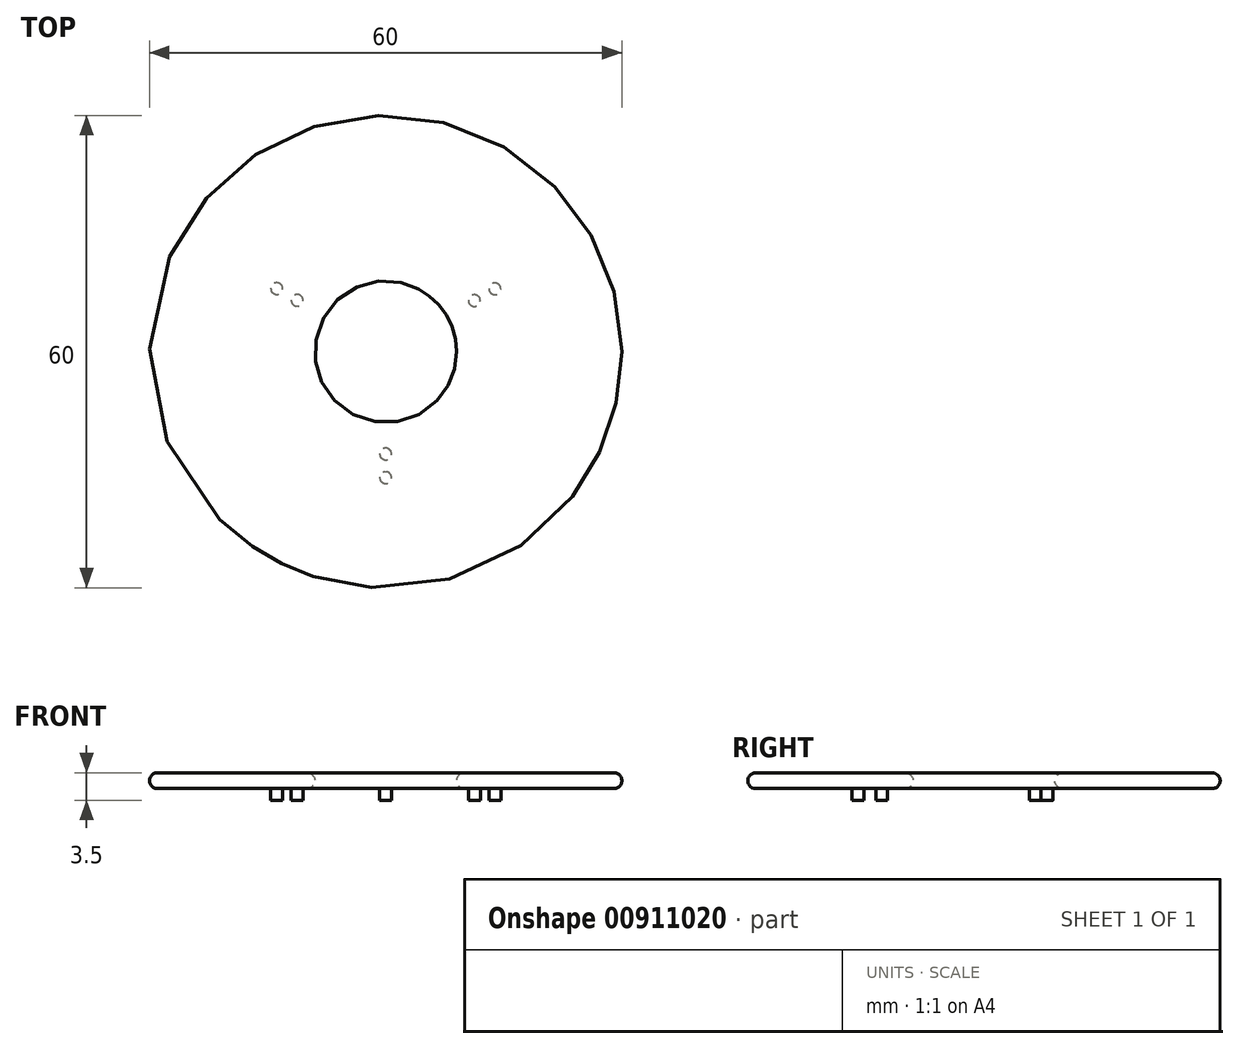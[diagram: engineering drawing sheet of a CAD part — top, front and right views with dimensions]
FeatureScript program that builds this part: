
annotation { "Feature Type Name" : "Feature", "Feature Type Description" : "" }
export const myFeature = defineFeature(function(context is Context, id is Id, definition is map)
    precondition{}
    {
        {
            var Q0;
            Q0=qCreatedBy(makeId("Top.planeOp"),FACE);
            var sketch = newSketch(context, id + "F0", { "sketchPlane" : qUnion([Q0])});
            skCircle(sketch, "E0", {"center": v(0, 0) * mm, "radius": 30 * mm});
            skCircle(sketch, "E1", {"center": v(0, 0) * mm, "radius": 9 * mm});
            skSolve(sketch);
        }
        {
            var Q0;
            Q0=makeQuery(id+"F0.imprint","IMPRINT",FACE,{"disambiguationData":[TD([[makeQuery(id+"F0.imprint","IMPRINT",EDGE,{"derivedFrom":sQuery(id+"F0.wireOp",EDGE,"E0")}),1.0]])]});
            extrude(context, id + "F1", {"entities" : qUnion([Q0]), "depth" : 2 * mm, "offsetDistance" : 25 * mm});
        }
        {
            var Q0;
            Q0=makeQuery(id+"F1.opExtrude","CAP_EDGE",EDGE,{"disambiguationData":[OSD([sQuery(id+"F0.wireOp",EDGE,"E1")])],"isStart":false});
            var Q1;
            Q1=makeQuery(id+"F1.opExtrude","CAP_EDGE",EDGE,{"disambiguationData":[OSD([sQuery(id+"F0.wireOp",EDGE,"E1")])],"isStart":true});
            var Q2;
            Q2=makeQuery(id+"F1.opExtrude","CAP_EDGE",EDGE,{"disambiguationData":[OSD([sQuery(id+"F0.wireOp",EDGE,"E0")])],"isStart":true});
            var Q3;
            Q3=makeQuery(id+"F1.opExtrude","CAP_EDGE",EDGE,{"disambiguationData":[OSD([sQuery(id+"F0.wireOp",EDGE,"E0")])],"isStart":false});
            fillet(context, id + "F2", {"entities" : qUnion([Q0, Q1, Q2, Q3]), "tangentPropagation" : true, "radius" : 1 * mm, "defaultsChanged" : false, "vertexSettings" : [], "allowEdgeOverflow" : false});
        }
        {
            var Q0;
            Q0=qCreatedBy(makeId("Top.planeOp"),FACE);
            var sketch = newSketch(context, id + "F3", { "sketchPlane" : qUnion([Q0])});
            skCircle(sketch, "E2.cCircle", {"center": v(0, 0) * mm, "radius": 13 * mm, "construction": true});
            skLineSegment(sketch, "E2.0", {"start": v(11.26, 6.49) * mm, "end": v(-0.01, -13) * mm});
            skLineSegment(sketch, "E2.1", {"start": v(-0.01, -13) * mm, "end": v(-11.25, 6.51) * mm});
            skLineSegment(sketch, "E2.2", {"start": v(-11.25, 6.51) * mm, "end": v(11.26, 6.49) * mm});
            skCircle(sketch, "E3", {"center": v(-11.25, 6.51) * mm, "radius": 0.75 * mm});
            skCircle(sketch, "E4", {"center": v(11.26, 6.49) * mm, "radius": 0.75 * mm});
            skCircle(sketch, "E5", {"center": v(-0.01, -13) * mm, "radius": 0.75 * mm});
            skCircle(sketch, "E6.cCircle", {"center": v(0, 0) * mm, "radius": 16 * mm, "construction": true});
            skLineSegment(sketch, "E6.0", {"start": v(13.86, 7.99) * mm, "end": v(-0.01, -16) * mm});
            skLineSegment(sketch, "E6.1", {"start": v(-0.01, -16) * mm, "end": v(-13.85, 8.01) * mm});
            skLineSegment(sketch, "E6.2", {"start": v(-13.85, 8.01) * mm, "end": v(13.86, 7.99) * mm});
            skCircle(sketch, "E7", {"center": v(-13.85, 8.01) * mm, "radius": 0.75 * mm});
            skCircle(sketch, "E8", {"center": v(13.86, 7.99) * mm, "radius": 0.75 * mm});
            skCircle(sketch, "E9", {"center": v(-0.01, -16) * mm, "radius": 0.75 * mm});
            skSolve(sketch);
        }
        {
            var Q0;
            {var subQ0=sQuery(id+"F3.wireOp",EDGE,"E6.2");var subQ1=sQuery(id+"F3.wireOp",EDGE,"E6.0");var subQ2=makeQuery(id+"F3.imprint","INTERSECT",VERTEX,{"derivedFrom":[subQ1,subQ0]});Q0=makeQuery(id+"F3.imprint","IMPRINT",FACE,{"disambiguationData":[TD([[makeQuery(id+"F3.imprint","IMPRINT",EDGE,{"disambiguationData":[TD([[subQ2,-1.0]])],"derivedFrom":subQ1}),1.0]])]});}
            var Q1;
            {var subQ0=sQuery(id+"F3.wireOp",EDGE,"E2.2");var subQ1=sQuery(id+"F3.wireOp",EDGE,"E2.0");var subQ2=makeQuery(id+"F3.imprint","INTERSECT",VERTEX,{"derivedFrom":[subQ1,subQ0]});Q1=makeQuery(id+"F3.imprint","IMPRINT",FACE,{"disambiguationData":[TD([[makeQuery(id+"F3.imprint","IMPRINT",EDGE,{"disambiguationData":[TD([[subQ2,-1.0]])],"derivedFrom":subQ1}),1.0]])]});}
            var Q2;
            {var subQ0=sQuery(id+"F3.wireOp",EDGE,"E6.2");var subQ1=sQuery(id+"F3.wireOp",EDGE,"E6.1");var subQ2=makeQuery(id+"F3.imprint","INTERSECT",VERTEX,{"derivedFrom":[subQ1,subQ0]});Q2=makeQuery(id+"F3.imprint","IMPRINT",FACE,{"disambiguationData":[TD([[makeQuery(id+"F3.imprint","IMPRINT",EDGE,{"disambiguationData":[TD([[subQ2,1.0]])],"derivedFrom":subQ1}),-1.0]])]});}
            var Q3;
            {var subQ0=sQuery(id+"F3.wireOp",EDGE,"E6.2");var subQ1=sQuery(id+"F3.wireOp",EDGE,"E6.1");var subQ2=makeQuery(id+"F3.imprint","INTERSECT",VERTEX,{"derivedFrom":[subQ1,subQ0]});Q3=makeQuery(id+"F3.imprint","IMPRINT",FACE,{"disambiguationData":[TD([[makeQuery(id+"F3.imprint","IMPRINT",EDGE,{"disambiguationData":[TD([[subQ2,1.0]])],"derivedFrom":subQ1}),1.0]])]});}
            var Q4;
            {var subQ0=sQuery(id+"F3.wireOp",EDGE,"E2.2");var subQ1=sQuery(id+"F3.wireOp",EDGE,"E2.1");var subQ2=makeQuery(id+"F3.imprint","INTERSECT",VERTEX,{"derivedFrom":[subQ1,subQ0]});Q4=makeQuery(id+"F3.imprint","IMPRINT",FACE,{"disambiguationData":[TD([[makeQuery(id+"F3.imprint","IMPRINT",EDGE,{"disambiguationData":[TD([[subQ2,1.0]])],"derivedFrom":subQ1}),1.0]])]});}
            var Q5;
            {var subQ0=sQuery(id+"F3.wireOp",EDGE,"E2.2");var subQ1=sQuery(id+"F3.wireOp",EDGE,"E2.1");var subQ2=makeQuery(id+"F3.imprint","INTERSECT",VERTEX,{"derivedFrom":[subQ1,subQ0]});Q5=makeQuery(id+"F3.imprint","IMPRINT",FACE,{"disambiguationData":[TD([[makeQuery(id+"F3.imprint","IMPRINT",EDGE,{"disambiguationData":[TD([[subQ2,1.0]])],"derivedFrom":subQ1}),-1.0]])]});}
            var Q6;
            {var subQ0=sQuery(id+"F3.wireOp",EDGE,"E2.2");var subQ1=sQuery(id+"F3.wireOp",EDGE,"E2.0");var subQ2=makeQuery(id+"F3.imprint","INTERSECT",VERTEX,{"derivedFrom":[subQ1,subQ0]});Q6=makeQuery(id+"F3.imprint","IMPRINT",FACE,{"disambiguationData":[TD([[makeQuery(id+"F3.imprint","IMPRINT",EDGE,{"disambiguationData":[TD([[subQ2,-1.0]])],"derivedFrom":subQ1}),-1.0]])]});}
            var Q7;
            {var subQ0=sQuery(id+"F3.wireOp",EDGE,"E6.2");var subQ1=sQuery(id+"F3.wireOp",EDGE,"E6.0");var subQ2=makeQuery(id+"F3.imprint","INTERSECT",VERTEX,{"derivedFrom":[subQ1,subQ0]});Q7=makeQuery(id+"F3.imprint","IMPRINT",FACE,{"disambiguationData":[TD([[makeQuery(id+"F3.imprint","IMPRINT",EDGE,{"disambiguationData":[TD([[subQ2,-1.0]])],"derivedFrom":subQ1}),-1.0]])]});}
            var Q8;
            {var subQ0=sQuery(id+"F3.wireOp",EDGE,"E2.1");var subQ1=sQuery(id+"F3.wireOp",EDGE,"E2.0");var subQ2=makeQuery(id+"F3.imprint","INTERSECT",VERTEX,{"derivedFrom":[subQ1,subQ0]});Q8=makeQuery(id+"F3.imprint","IMPRINT",FACE,{"disambiguationData":[TD([[makeQuery(id+"F3.imprint","IMPRINT",EDGE,{"disambiguationData":[TD([[subQ2,1.0]])],"derivedFrom":subQ1}),1.0]])]});}
            var Q9;
            {var subQ0=sQuery(id+"F3.wireOp",EDGE,"E2.1");var subQ1=sQuery(id+"F3.wireOp",EDGE,"E2.0");var subQ2=makeQuery(id+"F3.imprint","INTERSECT",VERTEX,{"derivedFrom":[subQ1,subQ0]});Q9=makeQuery(id+"F3.imprint","IMPRINT",FACE,{"disambiguationData":[TD([[makeQuery(id+"F3.imprint","IMPRINT",EDGE,{"disambiguationData":[TD([[subQ2,1.0]])],"derivedFrom":subQ1}),-1.0]])]});}
            var Q10;
            {var subQ0=sQuery(id+"F3.wireOp",EDGE,"E6.1");var subQ1=sQuery(id+"F3.wireOp",EDGE,"E6.0");var subQ2=makeQuery(id+"F3.imprint","INTERSECT",VERTEX,{"derivedFrom":[subQ1,subQ0]});Q10=makeQuery(id+"F3.imprint","IMPRINT",FACE,{"disambiguationData":[TD([[makeQuery(id+"F3.imprint","IMPRINT",EDGE,{"disambiguationData":[TD([[subQ2,1.0]])],"derivedFrom":subQ1}),-1.0]])]});}
            var Q11;
            {var subQ0=sQuery(id+"F3.wireOp",EDGE,"E6.1");var subQ1=sQuery(id+"F3.wireOp",EDGE,"E6.0");var subQ2=makeQuery(id+"F3.imprint","INTERSECT",VERTEX,{"derivedFrom":[subQ1,subQ0]});Q11=makeQuery(id+"F3.imprint","IMPRINT",FACE,{"disambiguationData":[TD([[makeQuery(id+"F3.imprint","IMPRINT",EDGE,{"disambiguationData":[TD([[subQ2,1.0]])],"derivedFrom":subQ1}),1.0]])]});}
            var Q12;
            Q12=sQuery(id+"F3.wireOp",EDGE,"E4");
            var Q13;
            Q13=sQuery(id+"F3.wireOp",EDGE,"E3");
            var Q14;
            Q14=sQuery(id+"F3.wireOp",EDGE,"E5");
            var Q15;
            Q15=sQuery(id+"F3.wireOp",EDGE,"E9");
            var Q16;
            Q16=sQuery(id+"F3.wireOp",EDGE,"E7");
            var Q17;
            Q17=sQuery(id+"F3.wireOp",EDGE,"E8");
            extrude(context, id + "F4", {"entities" : qUnion([Q0, Q1, Q2, Q3, Q4, Q5, Q6, Q7, Q8, Q9, Q10, Q11]), "surfaceOperationType" : NewSurfaceOperationType.ADD, "surfaceEntities" : qUnion([Q12, Q13, Q14, Q15, Q16, Q17]), "oppositeDirection" : true, "depth" : 1.5 * mm, "offsetDistance" : 25 * mm});
        }
    });
